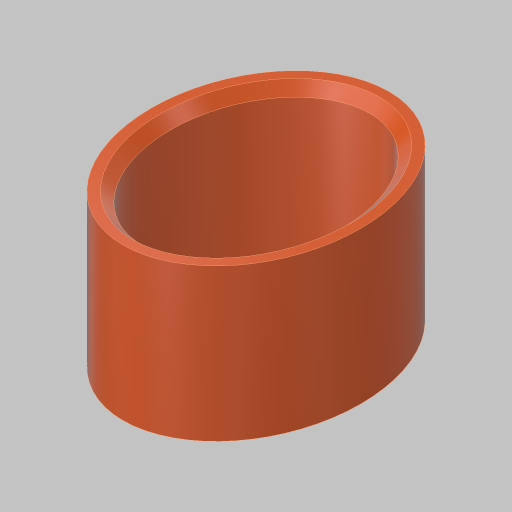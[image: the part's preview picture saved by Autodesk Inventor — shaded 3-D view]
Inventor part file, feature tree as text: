
AUTODESK INVENTOR PART (.ipt)
format: ipt  version: 2023.5 (Build 275446000, 446)  size: 138,752 bytes
history: native  units: in
note: dims shown in document units (in); Inventor stores cm internally (conversion verified against a paired STEP export)
features: extrude x1, chamfer x1, sketch x1
ambient origin geometry x8: Origin, YZ Plane, XZ Plane, XY Plane, X Axis, Y Axis, Z Axis, Center Point
bodies: Solid1 (feature_tree)
feature tree (3):
  extrude  "Extrusion1"  Depth=0.875in
  chamfer  "Chamfer1"  Distance=0.125in
  sketch  "Sketch1"  dims[d0=0.6875in d1=0.875in d2=0.125in d3=1.0in d4=0.0in d5=0.0625in d6=0.125in d7=45.0deg]
